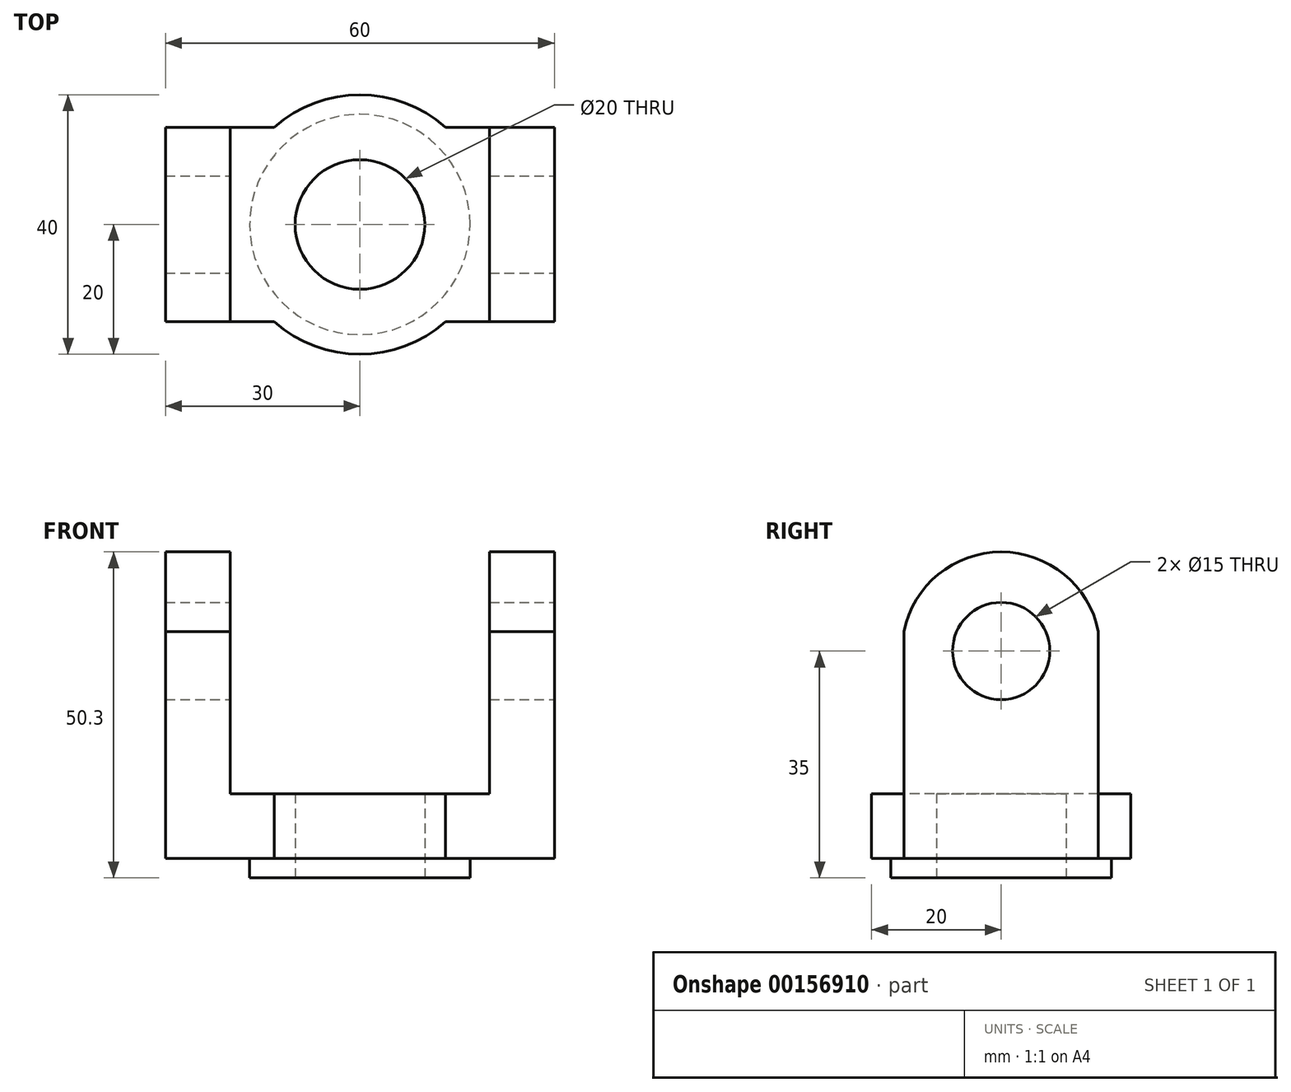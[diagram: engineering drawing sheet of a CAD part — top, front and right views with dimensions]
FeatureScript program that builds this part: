
annotation { "Feature Type Name" : "Feature", "Feature Type Description" : "" }
export const myFeature = defineFeature(function(context is Context, id is Id, definition is map)
    precondition{}
    {
        {
            var Q0;
            Q0=qCreatedBy(makeId("Top.planeOp"),FACE);
            var sketch = newSketch(context, id + "F0", { "sketchPlane" : qUnion([Q0])});
            skLineSegment(sketch, "E0.bottom", {"start": v(0, 0) * mm, "end": v(60, 0) * mm});
            skLineSegment(sketch, "E0.top", {"start": v(0, 30) * mm, "end": v(60, 30) * mm});
            skLineSegment(sketch, "E0.left", {"start": v(0, 0) * mm, "end": v(0, 30) * mm});
            skLineSegment(sketch, "E0.right", {"start": v(60, 0) * mm, "end": v(60, 30) * mm});
            skArc(sketch, "E1", {"start": v(43.23, 30) * mm, "mid": v(30, 35) * mm, "end": v(16.77, 30) * mm});
            skArc(sketch, "E2", {"start": v(16.77, 0) * mm, "mid": v(30, -5) * mm, "end": v(43.23, 0) * mm});
            skCircle(sketch, "E3", {"center": v(30, 15) * mm, "radius": 10 * mm});
            skPoint(sketch, "E4", {"position": v(30, 30) * mm});
            skSolve(sketch);
        }
        {
            var Q0;
            {var subQ0=sQuery(id+"F0.wireOp",EDGE,"E2");Q0=makeQuery(id+"F0.imprint","IMPRINT",FACE,{"disambiguationData":[TD([[makeQuery(id+"F0.imprint","IMPRINT",EDGE,{"derivedFrom":subQ0}),1.0]])]});}
            var Q1;
            {var subQ0=sQuery(id+"F0.wireOp",EDGE,"E0.left");Q1=makeQuery(id+"F0.imprint","IMPRINT",FACE,{"disambiguationData":[TD([[makeQuery(id+"F0.imprint","IMPRINT",EDGE,{"derivedFrom":subQ0}),-1.0]])]});}
            var Q2;
            {var subQ0=sQuery(id+"F0.wireOp",EDGE,"E1");Q2=makeQuery(id+"F0.imprint","IMPRINT",FACE,{"disambiguationData":[TD([[makeQuery(id+"F0.imprint","IMPRINT",EDGE,{"derivedFrom":subQ0}),1.0]])]});}
            extrude(context, id + "F1", {"entities" : qUnion([Q0, Q1, Q2]), "depth" : 50 * mm});
        }
        {
            var Q0;
            Q0=makeQuery(id+"F1.opExtrude","CAP_FACE",FACE,{"disambiguationData":[OSD([sQuery(id+"F0.wireOp",EDGE,"E0.bottom"),sQuery(id+"F0.wireOp",EDGE,"E0.top"),sQuery(id+"F0.wireOp",EDGE,"E0.left"),sQuery(id+"F0.wireOp",EDGE,"E0.right"),sQuery(id+"F0.wireOp",EDGE,"E1"),sQuery(id+"F0.wireOp",EDGE,"E2"),sQuery(id+"F0.wireOp",EDGE,"E3")])],"isStart":false});
            var sketch = newSketch(context, id + "F2", { "sketchPlane" : qUnion([Q0])});
            skLineSegment(sketch, "E5.bottom", {"start": v(10, 35) * mm, "end": v(50, 35) * mm});
            skLineSegment(sketch, "E5.top", {"start": v(10, -5) * mm, "end": v(50, -5) * mm});
            skLineSegment(sketch, "E5.left", {"start": v(10, 35) * mm, "end": v(10, -5) * mm});
            skLineSegment(sketch, "E5.right", {"start": v(50, 35) * mm, "end": v(50, -5) * mm});
            skSolve(sketch);
        }
        {
            var Q0;
            Q0=makeQuery(id+"F2.imprint","IMPRINT",FACE,{"disambiguationData":[TD([[makeQuery(id+"F2.imprint","IMPRINT",EDGE,{"derivedFrom":makeQuery(id+"F1.opExtrude","CAP_EDGE",EDGE,{"disambiguationData":[OSD([sQuery(id+"F0.wireOp",EDGE,"E3")])],"isStart":false})}),-1.0]])]});
            extrude(context, id + "F3", {"entities" : qUnion([Q0]), "operationType" : NewBodyOperationType.REMOVE, "oppositeDirection" : true, "depth" : 40 * mm});
        }
        {
            var Q0;
            Q0=makeQuery(id+"F1.opExtrude","SWEPT_FACE",FACE,{"disambiguationData":[OSD([sQuery(id+"F0.wireOp",EDGE,"E0.right")])]});
            var sketch = newSketch(context, id + "F4", { "sketchPlane" : qUnion([Q0])});
            skLineSegment(sketch, "E6.bottom", {"start": v(0, 50) * mm, "end": v(30, 50) * mm});
            skLineSegment(sketch, "E6.top", {"start": v(0, 10) * mm, "end": v(30, 10) * mm});
            skLineSegment(sketch, "E6.left", {"start": v(0, 50) * mm, "end": v(0, 10) * mm});
            skLineSegment(sketch, "E6.right", {"start": v(30, 50) * mm, "end": v(30, 10) * mm});
            skCircle(sketch, "E7", {"center": v(15, 32) * mm, "radius": 7.5 * mm});
            skArc(sketch, "E8", {"start": v(30, 35) * mm, "mid": v(15, 47.3) * mm, "end": v(0, 35) * mm});
            skSolve(sketch);
        }
        {
            var Q0;
            {var subQ0=sQuery(id+"F4.wireOp",EDGE,"E6.bottom");Q0=makeQuery(id+"F4.imprint","IMPRINT",FACE,{"disambiguationData":[TD([[makeQuery(id+"F4.imprint","IMPRINT",EDGE,{"derivedFrom":subQ0}),-1.0]])]});}
            var Q1;
            Q1=makeQuery(id+"F4.imprint","IMPRINT",FACE,{"disambiguationData":[TD([[makeQuery(id+"F4.imprint","IMPRINT",EDGE,{"derivedFrom":sQuery(id+"F4.wireOp",EDGE,"E7")}),1.0]])]});
            extrude(context, id + "F5", {"entities" : qUnion([Q0, Q1]), "operationType" : NewBodyOperationType.REMOVE, "endBound" : BoundingType.THROUGH_ALL, "oppositeDirection" : true, "depth" : 25 * mm});
        }
        {
            var Q0;
            Q0=makeQuery(id+"F1.opExtrude","CAP_FACE",FACE,{"disambiguationData":[OSD([sQuery(id+"F0.wireOp",EDGE,"E0.bottom"),sQuery(id+"F0.wireOp",EDGE,"E0.top"),sQuery(id+"F0.wireOp",EDGE,"E0.left"),sQuery(id+"F0.wireOp",EDGE,"E0.right"),sQuery(id+"F0.wireOp",EDGE,"E1"),sQuery(id+"F0.wireOp",EDGE,"E2"),sQuery(id+"F0.wireOp",EDGE,"E3")])],"isStart":true});
            var sketch = newSketch(context, id + "F6", { "sketchPlane" : qUnion([Q0])});
            skCircle(sketch, "E9", {"center": v(30, -15) * mm, "radius": 17 * mm});
            skSolve(sketch);
        }
        {
            var Q0;
            Q0=makeQuery(id+"F6.imprint","IMPRINT",FACE,{"disambiguationData":[TD([[makeQuery(id+"F6.imprint","IMPRINT",EDGE,{"derivedFrom":sQuery(id+"F6.wireOp",EDGE,"E9")}),1.0]])]});
            extrude(context, id + "F7", {"entities" : qUnion([Q0]), "operationType" : NewBodyOperationType.ADD, "depth" : 3 * mm});
        }
    });
